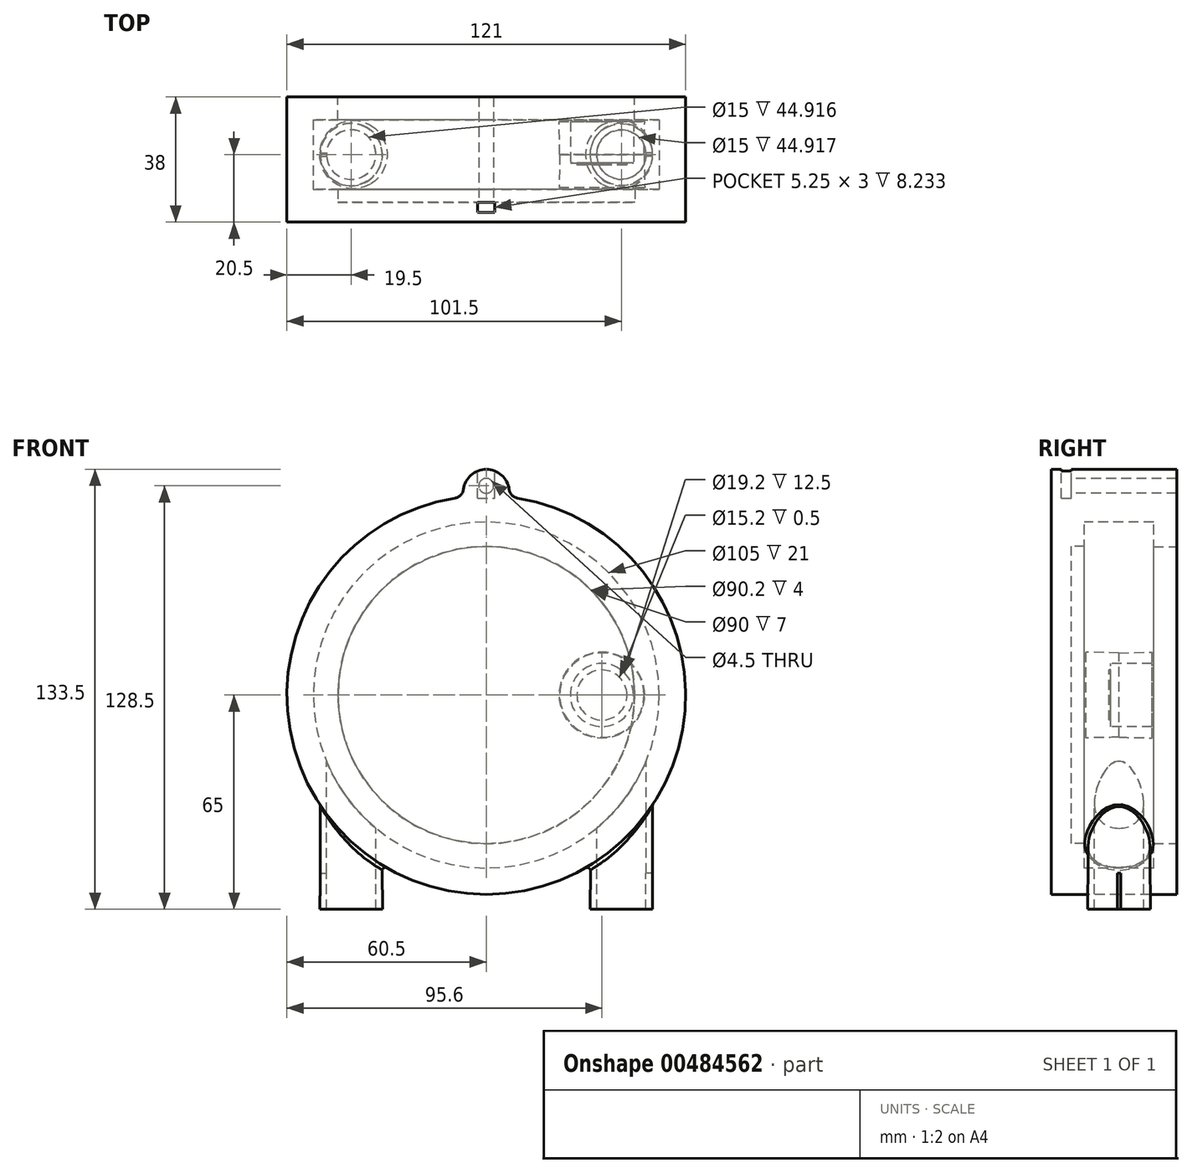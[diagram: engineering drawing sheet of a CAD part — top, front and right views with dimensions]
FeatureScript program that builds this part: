
annotation { "Feature Type Name" : "Feature", "Feature Type Description" : "" }
export const myFeature = defineFeature(function(context is Context, id is Id, definition is map)
    precondition{}
    {
        {
            var Q0;
            Q0=qCreatedBy(makeId("Top.planeOp"),FACE);
            var sketch = newSketch(context, id + "F0", { "sketchPlane" : qUnion([Q0])});
            skLineSegment(sketch, "E0", {"start": v(0, 0) * mm, "end": v(0, 21) * mm, "construction": true});
            skLineSegment(sketch, "E1", {"start": v(0, 28) * mm, "end": v(60.5, 28) * mm});
            skLineSegment(sketch, "E2", {"start": v(60.5, 28) * mm, "end": v(60.5, 21) * mm});
            skLineSegment(sketch, "E3", {"start": v(60.5, 21) * mm, "end": v(0, 21) * mm});
            skLineSegment(sketch, "E4", {"start": v(0, 28) * mm, "end": v(0, 21) * mm});
            skLineSegment(sketch, "E5", {"start": v(60.5, 21) * mm, "end": v(60.5, -10) * mm});
            skLineSegment(sketch, "E6", {"start": v(60.5, -10) * mm, "end": v(0, -10) * mm});
            skLineSegment(sketch, "E7", {"start": v(0, -10) * mm, "end": v(0, -4) * mm});
            skLineSegment(sketch, "E8", {"start": v(45.1, 0) * mm, "end": v(52.5, 0) * mm});
            skLineSegment(sketch, "E9", {"start": v(52.5, 0) * mm, "end": v(52.5, 21) * mm});
            skLineSegment(sketch, "E10", {"start": v(48.1, 0.5) * mm, "end": v(35.1, 0.5) * mm});
            skLineSegment(sketch, "E11", {"start": v(35.1, 0.5) * mm, "end": v(35.1, 7.5) * mm});
            skLineSegment(sketch, "E12", {"start": v(42.7, 8) * mm, "end": v(44.7, 8) * mm});
            skLineSegment(sketch, "E13", {"start": v(44.7, 8) * mm, "end": v(44.7, 20.5) * mm});
            skLineSegment(sketch, "E14", {"start": v(44.7, 20.5) * mm, "end": v(48.1, 20.5) * mm});
            skPoint(sketch, "E15", {"position": v(47.9, 10.5) * mm});
            skLineSegment(sketch, "E16", {"start": v(48.1, 20.5) * mm, "end": v(47.9, 10.5) * mm});
            skLineSegment(sketch, "E17", {"start": v(48.1, 0.5) * mm, "end": v(47.9, 10.5) * mm});
            skLineSegment(sketch, "E18", {"start": v(42.7, 8) * mm, "end": v(42.7, 7.5) * mm});
            skLineSegment(sketch, "E19", {"start": v(42.7, 7.5) * mm, "end": v(35.1, 7.5) * mm});
            skLineSegment(sketch, "E20", {"start": v(35.1, 7.5) * mm, "end": v(35.1, 11.5) * mm, "construction": true});
            skLineSegment(sketch, "E21", {"start": v(0, -4) * mm, "end": v(45.1, -4) * mm});
            skLineSegment(sketch, "E22", {"start": v(45.1, -4) * mm, "end": v(45.1, 0) * mm});
            skSolve(sketch);
        }
        {
            var Q0;
            {var subQ0=sQuery(id+"F0.wireOp",EDGE,"E5");Q0=makeQuery(id+"F0.imprint","IMPRINT",FACE,{"disambiguationData":[TD([[makeQuery(id+"F0.imprint","IMPRINT",EDGE,{"derivedFrom":subQ0}),-1.0]])]});}
            var Q1;
            Q1=sQuery(id+"F0.wireOp",EDGE,"E0");
            revolve(context, id + "F1", {"entities" : qUnion([Q0]), "axis" : qUnion([Q1]), "revolveType" : RevolveType.FULL});
        }
        {
            var Q0;
            Q0=makeQuery(id+"F0.imprint","IMPRINT",FACE,{"disambiguationData":[TD([[makeQuery(id+"F0.imprint","IMPRINT",EDGE,{"derivedFrom":sQuery(id+"F0.wireOp",EDGE,"E1")}),-1.0]])]});
            var Q1;
            Q1=sQuery(id+"F0.wireOp",EDGE,"E4");
            revolve(context, id + "F2", {"entities" : qUnion([Q0]), "axis" : qUnion([Q1]), "revolveType" : RevolveType.FULL});
        }
        {
            var Q0;
            {var subQ0=sQuery(id+"F0.wireOp",EDGE,"E3");Q0=makeQuery(id+"F1.opRevolve","SWEPT_FACE",FACE,{"disambiguationData":[OSD([subQ0]),TDD([makeQuery(id+"F0.imprint","IMPRINT",EDGE,{"disambiguationData":[TD([[makeQuery(id+"F0.imprint","INTERSECT",VERTEX,{"derivedFrom":[sQuery(id+"F0.wireOp",EDGE,"E2"),subQ0,sQuery(id+"F0.wireOp",EDGE,"E5")]}),-1.0]])],"derivedFrom":subQ0})])]});}
            var sketch = newSketch(context, id + "F3", { "sketchPlane" : qUnion([Q0])});
            skArc(sketch, "E23", {"start": v(6.95, 62.35) * mm, "mid": v(0, 68.5) * mm, "end": v(-6.95, 62.35) * mm});
            skArc(sketch, "E24", {"start": v(-9.46, 59.76) * mm, "mid": v(-7.77, 60.64) * mm, "end": v(-6.95, 62.35) * mm});
            skLineSegment(sketch, "E25", {"start": v(0, 0) * mm, "end": v(0, 56.73) * mm, "construction": true});
            skArc(sketch, "E26.MirrorCS", {"start": v(9.46, 59.76) * mm, "mid": v(7.77, 60.64) * mm, "end": v(6.95, 62.35) * mm});
            skArc(sketch, "E27", {"start": v(9.46, 59.76) * mm, "mid": v(0, 60.5) * mm, "end": v(-9.46, 59.76) * mm});
            skCircle(sketch, "E28", {"center": v(0, 63.5) * mm, "radius": 2.25 * mm});
            skSolve(sketch);
        }
        {
            var Q0;
            Q0=makeQuery(id+"F3.imprint","IMPRINT",FACE,{"disambiguationData":[TD([[makeQuery(id+"F3.imprint","IMPRINT",EDGE,{"derivedFrom":sQuery(id+"F3.wireOp",EDGE,"E23")}),1.0]])]});
            var Q1;
            Q1=makeQuery(id+"F2.opRevolve","SWEPT_FACE",FACE,{"disambiguationData":[OSD([sQuery(id+"F0.wireOp",EDGE,"E1")])]});
            extrude(context, id + "F4", {"entities" : qUnion([Q0]), "operationType" : NewBodyOperationType.ADD, "endBound" : BoundingType.UP_TO_SURFACE, "endBoundEntityFace" : qUnion([Q1]), "depth" : 25 * mm, "offsetDistance" : 25 * mm});
        }
        {
            var Q0;
            Q0=makeQuery(id+"F3.imprint","IMPRINT",FACE,{"disambiguationData":[TD([[makeQuery(id+"F3.imprint","IMPRINT",EDGE,{"derivedFrom":sQuery(id+"F3.wireOp",EDGE,"E23")}),1.0]])]});
            var Q1;
            Q1=makeQuery(id+"F3.imprint","IMPRINT",FACE,{"disambiguationData":[TD([[makeQuery(id+"F3.imprint","IMPRINT",EDGE,{"derivedFrom":sQuery(id+"F3.wireOp",EDGE,"E28")}),1.0]])]});
            var Q2;
            Q2=makeQuery(id+"F1.opRevolve","SWEPT_FACE",FACE,{"disambiguationData":[OSD([sQuery(id+"F0.wireOp",EDGE,"E6")])]});
            extrude(context, id + "F5", {"entities" : qUnion([Q0, Q1]), "operationType" : NewBodyOperationType.ADD, "endBound" : BoundingType.UP_TO_SURFACE, "oppositeDirection" : true, "endBoundEntityFace" : qUnion([Q2]), "depth" : 25 * mm, "offsetDistance" : 25 * mm});
        }
        {
            var Q0;
            Q0=sQuery(id+"F3.wireOp",EDGE,"E23");
            cPoint(context, id + "F6", {"entities" : qUnion([Q0]), "parameter" : 0.5});
        }
        {
            var Q0;
            Q0 = qCreatedBy(id + "F6" ,VERTEX);
            var Q1;
            Q1=sQuery(id+"F3.wireOp",EDGE,"E25");
            cPlane(context, id + "F7", {"entities" : qUnion([Q0, Q1]), "cplaneType" : CPlaneType.LINE_POINT, "offset" : 25 * mm, "width" : 150 * mm, "height" : 150 * mm});
        }
        {
            var Q0;
            Q0=qCreatedBy(id+"F7.planeOp",FACE);
            var sketch = newSketch(context, id + "F8", { "sketchPlane" : qUnion([Q0])});
            skLineSegment(sketch, "E29.bottom", {"start": v(-2.62, -7) * mm, "end": v(2.62, -7) * mm});
            skLineSegment(sketch, "E29.top", {"start": v(-2.62, -4) * mm, "end": v(2.62, -4) * mm});
            skLineSegment(sketch, "E29.left", {"start": v(-2.62, -7) * mm, "end": v(-2.62, -4) * mm});
            skLineSegment(sketch, "E29.right", {"start": v(2.63, -7) * mm, "end": v(2.63, -4) * mm});
            skLineSegment(sketch, "E30", {"start": v(0, -4) * mm, "end": v(0, 0) * mm, "construction": true});
            skSolve(sketch);
        }
        {
            var Q0;
            Q0 = qSketchRegion(id + "F8", true);
            var Q1;
            Q1=makeQuery(id+"F5.opExtrude","CAP_VERTEX",VERTEX,{"disambiguationData":[OSD([sQuery(id+"F0.wireOp",EDGE,"E2"),sQuery(id+"F0.wireOp",EDGE,"E3"),sQuery(id+"F0.wireOp",EDGE,"E5"),sQuery(id+"F0.wireOp",EDGE,"E6"),sQuery(id+"F3.wireOp",EDGE,"E24"),sQuery(id+"F3.wireOp",EDGE,"E27")])],"isStart":false});
            extrude(context, id + "F9", {"entities" : qUnion([Q0]), "operationType" : NewBodyOperationType.REMOVE, "endBound" : BoundingType.UP_TO_VERTEX, "oppositeDirection" : true, "endBoundEntityVertex" : qUnion([Q1]), "depth" : 8 * mm});
        }
        {
            var Q0;
            Q0=makeQuery(id+"F3.imprint","IMPRINT",FACE,{"disambiguationData":[TD([[makeQuery(id+"F3.imprint","IMPRINT",EDGE,{"derivedFrom":sQuery(id+"F3.wireOp",EDGE,"E28")}),1.0]])]});
            var Q1;
            Q1=makeQuery(id+"F9.boolean.opBoolean","COPY",FACE,{"derivedFrom":makeQuery(id+"F9.opExtrude","SWEPT_FACE",FACE,{"disambiguationData":[OSD([sQuery(id+"F8.wireOp",EDGE,"E29.top")])]})});
            extrude(context, id + "F10", {"entities" : qUnion([Q0]), "operationType" : NewBodyOperationType.REMOVE, "endBound" : BoundingType.UP_TO_SURFACE, "oppositeDirection" : true, "depth" : 25 * mm, "endBoundEntityFace" : qUnion([Q1]), "offsetDistance" : 25 * mm});
        }
        {
            var Q0;
            Q0=sQuery(id+"F0.wireOp",EDGE,"E0");
            cPoint(context, id + "F11", {"entities" : qUnion([Q0]), "parameter" : 0.5});
        }
        {
            var Q0;
            Q0 = qCreatedBy(id + "F11" ,VERTEX);
            var Q1;
            Q1=sQuery(id+"F0.wireOp",EDGE,"E0");
            cPlane(context, id + "F12", {"entities" : qUnion([Q0, Q1]), "cplaneType" : CPlaneType.LINE_POINT, "offset" : 25 * mm, "width" : 150 * mm, "height" : 150 * mm});
        }
        {
            var Q0;
            {var subQ0=sQuery(id+"F0.wireOp",EDGE,"E1");Q0=makeQuery(id+"F8Ouq5LeF6Cl571_2.3.F4.boolean.opBoolean","MERGE",FACE,{"derivedFrom":[makeQuery(id+"F8Ouq5LeF6Cl571_2.2.F4.boolean.opBoolean","MERGE",FACE,{"derivedFrom":[makeQuery(id+"F8Ouq5LeF6Cl571_2.1.F4.boolean.opBoolean","MERGE",FACE,{"derivedFrom":[makeQuery(id+"F4.boolean.opBoolean","MERGE",FACE,{"derivedFrom":[makeQuery(id+"F2.opRevolve","SWEPT_FACE",FACE,{"disambiguationData":[OSD([subQ0])]}),makeQuery(id+"F4.opExtrude","CAP_FACE",FACE,{"disambiguationData":[OSD([subQ0])],"isStart":false})]}),makeQuery(id+"F8Ouq5LeF6Cl571_2.1.F4.opExtrude","CAP_FACE",FACE,{"disambiguationData":[OSD([subQ0])],"isStart":false})]}),makeQuery(id+"F8Ouq5LeF6Cl571_2.2.F4.opExtrude","CAP_FACE",FACE,{"disambiguationData":[OSD([subQ0])],"isStart":false})]}),makeQuery(id+"F8Ouq5LeF6Cl571_2.3.F4.opExtrude","CAP_FACE",FACE,{"disambiguationData":[OSD([subQ0])],"isStart":false})]});}
            var sketch = newSketch(context, id + "F13", { "sketchPlane" : qUnion([Q0])});
            skCircle(sketch, "E31", {"center": v(0, 0) * mm, "radius": 45 * mm});
            skSolve(sketch);
        }
        {
            var Q0;
            Q0=makeQuery(id+"F13.imprint","IMPRINT",FACE,{"disambiguationData":[TD([[makeQuery(id+"F13.imprint","IMPRINT",EDGE,{"derivedFrom":sQuery(id+"F13.wireOp",EDGE,"E31")}),1.0]])]});
            extrude(context, id + "F14", {"entities" : qUnion([Q0]), "operationType" : NewBodyOperationType.REMOVE, "endBound" : BoundingType.UP_TO_NEXT, "oppositeDirection" : true, "depth" : 25 * mm, "offsetDistance" : 25 * mm});
        }
        {
            var Q0;
            Q0=qCreatedBy(id+"F12.planeOp",FACE);
            var sketch = newSketch(context, id + "F15", { "sketchPlane" : qUnion([Q0])});
            skLineSegment(sketch, "E32", {"start": v(-50.39, -50) * mm, "end": v(-41, -50) * mm});
            skLineSegment(sketch, "E33", {"start": v(-41, -50) * mm, "end": v(-41, -65) * mm, "construction": true});
            skLineSegment(sketch, "E34", {"start": v(-41, -65) * mm, "end": v(-50.5, -65) * mm});
            skLineSegment(sketch, "E35", {"start": v(-50.5, -65) * mm, "end": v(-50.39, -50) * mm});
            skLineSegment(sketch, "E36", {"start": v(-41, -65) * mm, "end": v(-41, -50) * mm});
            skLineSegment(sketch, "E37", {"start": v(-48.5, -50) * mm, "end": v(-48.5, -65) * mm});
            skSolve(sketch);
        }
        {
            var Q0;
            Q0=makeQuery(id+"F15.imprint","IMPRINT",FACE,{"disambiguationData":[TD([[makeQuery(id+"F15.imprint","IMPRINT",EDGE,{"derivedFrom":sQuery(id+"F15.wireOp",EDGE,"E32")}),-1.0]])]});
            var Q1;
            Q1=sQuery(id+"F15.wireOp",EDGE,"E35");
            var Q2;
            Q2=sQuery(id+"F15.wireOp",EDGE,"E32");
            var Q3;
            Q3=sQuery(id+"F15.wireOp",EDGE,"E34");
            var Q4;
            Q4=sQuery(id+"F15.wireOp",EDGE,"E33");
            revolve(context, id + "F16", {"operationType" : NewBodyOperationType.ADD, "entities" : qUnion([Q0]), "surfaceEntities" : qUnion([Q1, Q2, Q3]), "axis" : qUnion([Q4]), "revolveType" : RevolveType.FULL});
        }
        {
            var Q0;
            Q0=makeQuery(id+"F16.opRevolve","SWEPT_FACE",FACE,{"disambiguationData":[OSD([sQuery(id+"F15.wireOp",EDGE,"E32")])]});
            var Q1;
            Q1=makeQuery(id+"F1.opRevolve","SWEPT_FACE",FACE,{"disambiguationData":[OSD([sQuery(id+"F0.wireOp",EDGE,"E9")])]});
            extrude(context, id + "F17", {"entities" : qUnion([Q0]), "operationType" : NewBodyOperationType.ADD, "endBound" : BoundingType.UP_TO_SURFACE, "depth" : 25 * mm, "endBoundEntityFace" : qUnion([Q1]), "offsetDistance" : 25 * mm});
        }
        {
            var Q0;
            Q0=makeQuery(id+"F16.opRevolve","SWEPT_FACE",FACE,{"disambiguationData":[OSD([sQuery(id+"F15.wireOp",EDGE,"E34")])]});
            var sketch = newSketch(context, id + "F18", { "sketchPlane" : qUnion([Q0])});
            skLineSegment(sketch, "E38.bottom", {"start": v(50.5, -10) * mm, "end": v(41, -10) * mm});
            skLineSegment(sketch, "E38.top", {"start": v(50.5, -11) * mm, "end": v(41, -11) * mm});
            skLineSegment(sketch, "E38.left", {"start": v(50.5, -10) * mm, "end": v(50.5, -11) * mm});
            skLineSegment(sketch, "E38.right", {"start": v(41, -10) * mm, "end": v(41, -11) * mm});
            skSolve(sketch);
        }
        {
            var Q0;
            {var subQ0=sQuery(id+"F15.wireOp",EDGE,"E36");Q0=makeQuery(id+"F15.imprint","IMPRINT",FACE,{"disambiguationData":[TD([[makeQuery(id+"F15.imprint","IMPRINT",EDGE,{"derivedFrom":subQ0}),1.0]])]});}
            var Q1;
            Q1=sQuery(id+"F15.wireOp",EDGE,"E36");
            revolve(context, id + "F19", {"operationType" : NewBodyOperationType.REMOVE, "entities" : qUnion([Q0]), "axis" : qUnion([Q1]), "revolveType" : RevolveType.FULL, "oppositeDirection" : true});
        }
        {
            var Q0;
            Q0=makeQuery(id+"F19.boolean.opBoolean","COPY",FACE,{"derivedFrom":makeQuery(id+"F19.opRevolve","SWEPT_FACE",FACE,{"disambiguationData":[OSD([sQuery(id+"F15.wireOp",EDGE,"E32")])]})});
            extrude(context, id + "F20", {"entities" : qUnion([Q0]), "operationType" : NewBodyOperationType.REMOVE, "endBound" : BoundingType.UP_TO_NEXT, "oppositeDirection" : true, "depth" : 25 * mm, "offsetDistance" : 25 * mm});
        }
        {
            var Q0;
            {var subQ4=sQuery(id+"F18.wireOp",EDGE,"E38.right");Q0=makeQuery(id+"F18.imprint","IMPRINT",FACE,{"disambiguationData":[TD([[makeQuery(id+"F18.imprint","IMPRINT",EDGE,{"derivedFrom":subQ4}),1.0]])]});}
            extrude(context, id + "F21", {"entities" : qUnion([Q0]), "operationType" : NewBodyOperationType.REMOVE, "oppositeDirection" : true, "depth" : 11 * mm, "offsetDistance" : 25 * mm});
        }
        {
            var Q0;
            {var subQ1=sQuery(id+"F3.wireOp",EDGE,"E26.MirrorCS");var subQ2=sQuery(id+"F3.wireOp",EDGE,"E24");var subQ10=makeQuery(id+"F8Ouq5LeF6Cl571_2.1.F5.opExtrude","SWEPT_FACE",FACE,{"disambiguationData":[OSD([subQ2])]});Q0=makeQuery(id+"F17.boolean.opBoolean","INTERSECT",EDGE,{"derivedFrom":[makeQuery(id+"F8Ouq5LeF6Cl571_2.2.F5.boolean.opBoolean","SPLIT",FACE,{"disambiguationData":[TD([subQ10])],"derivedFrom":makeQuery(id+"F8Ouq5LeF6Cl571_2.1.F5.boolean.opBoolean","SPLIT",FACE,{"disambiguationData":[TD([makeQuery(id+"F5.opExtrude","SWEPT_FACE",FACE,{"disambiguationData":[OSD([subQ1])]})])],"derivedFrom":makeQuery(id+"F1.opRevolve","SWEPT_FACE",FACE,{"disambiguationData":[OSD([sQuery(id+"F0.wireOp",EDGE,"E5")])]})})}),makeQuery(id+"F17.opExtrude","SWEPT_FACE",FACE,{"disambiguationData":[OSD([sQuery(id+"F15.wireOp",EDGE,"E32"),sQuery(id+"F15.wireOp",EDGE,"E35")])]})]});}
            fillet(context, id + "F22", {"entities" : qUnion([Q0]), "radius" : 1 * mm, "tangentPropagation" : true, "allowEdgeOverflow" : false});
        }
        {
            var Q0;
            Q0=makeQuery(id+"F16.opRevolve","SWEPT_FACE",FACE,{"disambiguationData":[OSD([sQuery(id+"F15.wireOp",EDGE,"E35")])]});
            var Q1;
            Q1=makeQuery(id+"FTRnezzPuA4SQwe_3.1.F21.boolean.opBoolean","COPY",FACE,{"derivedFrom":makeQuery(id+"FTRnezzPuA4SQwe_3.1.F21.opExtrude","SWEPT_FACE",FACE,{"disambiguationData":[OSD([sQuery(id+"F18.wireOp",EDGE,"E38.bottom")])]})});
            var Q2;
            Q2=makeQuery(id+"F17.opExtrude","SWEPT_FACE",FACE,{"disambiguationData":[OSD([sQuery(id+"F15.wireOp",EDGE,"E32"),sQuery(id+"F15.wireOp",EDGE,"E35")])]});
            var Q3;
            Q3=makeQuery(id+"F22.opFillet","BLEND_FACE",FACE,{"disambiguationData":[OSD([sQuery(id+"F0.wireOp",EDGE,"E5"),sQuery(id+"F15.wireOp",EDGE,"E32"),sQuery(id+"F15.wireOp",EDGE,"E35")])]});
            var Q4;
            Q4=makeQuery(id+"FTRnezzPuA4SQwe_3.3.F21.boolean.opBoolean","COPY",FACE,{"derivedFrom":makeQuery(id+"FTRnezzPuA4SQwe_3.3.F21.opExtrude","SWEPT_FACE",FACE,{"disambiguationData":[OSD([sQuery(id+"F18.wireOp",EDGE,"E38.top")])]})});
            var Q5;
            Q5=makeQuery(id+"FTRnezzPuA4SQwe_3.1.F21.boolean.opBoolean","COPY",FACE,{"derivedFrom":makeQuery(id+"FTRnezzPuA4SQwe_3.1.F21.opExtrude","SWEPT_FACE",FACE,{"disambiguationData":[OSD([sQuery(id+"F18.wireOp",EDGE,"E38.top")])]})});
            var Q6;
            {var subQ0=makeQuery(id+"FTRnezzPuA4SQwe_3.1.F21.opExtrude","SWEPT_FACE",FACE,{"disambiguationData":[OSD([sQuery(id+"F18.wireOp",EDGE,"E38.top")])]});var subQ5=sQuery(id+"F18.wireOp",EDGE,"E38.bottom");Q6=makeQuery(id+"FTRnezzPuA4SQwe_3.2.F21.boolean.opBoolean","SPLIT",FACE,{"disambiguationData":[TD([makeQuery(id+"FTRnezzPuA4SQwe_3.1.F21.boolean.opBoolean","COPY",FACE,{"derivedFrom":subQ0})])],"derivedFrom":makeQuery(id+"FTRnezzPuA4SQwe_3.1.F21.boolean.opBoolean","SPLIT",FACE,{"disambiguationData":[TD([makeQuery(id+"F21.boolean.opBoolean","COPY",FACE,{"derivedFrom":makeQuery(id+"F21.opExtrude","SWEPT_FACE",FACE,{"disambiguationData":[OSD([subQ5])]})})])],"derivedFrom":makeQuery(id+"F16.opRevolve","SWEPT_FACE",FACE,{"disambiguationData":[OSD([sQuery(id+"F15.wireOp",EDGE,"E34")])]})})});}
            var Q7;
            Q7=makeQuery(id+"F21.boolean.opBoolean","COPY",FACE,{"derivedFrom":makeQuery(id+"F21.opExtrude","SWEPT_FACE",FACE,{"disambiguationData":[OSD([sQuery(id+"F18.wireOp",EDGE,"E38.top")])]})});
            var Q8;
            Q8=makeQuery(id+"FTRnezzPuA4SQwe_3.1.F21.boolean.opBoolean","SPLIT",FACE,{"disambiguationData":[TD([makeQuery(id+"F21.boolean.opBoolean","COPY",FACE,{"derivedFrom":makeQuery(id+"F21.opExtrude","SWEPT_FACE",FACE,{"disambiguationData":[OSD([sQuery(id+"F18.wireOp",EDGE,"E38.top")])]})})])],"derivedFrom":makeQuery(id+"F16.opRevolve","SWEPT_FACE",FACE,{"disambiguationData":[OSD([sQuery(id+"F15.wireOp",EDGE,"E34")])]})});
            var Q9;
            Q9=makeQuery(id+"FTRnezzPuA4SQwe_3.3.F21.boolean.opBoolean","COPY",FACE,{"derivedFrom":makeQuery(id+"FTRnezzPuA4SQwe_3.3.F21.opExtrude","SWEPT_FACE",FACE,{"disambiguationData":[OSD([sQuery(id+"F18.wireOp",EDGE,"E38.bottom")])]})});
            var Q10;
            Q10=makeQuery(id+"FTRnezzPuA4SQwe_3.2.F21.boolean.opBoolean","COPY",FACE,{"derivedFrom":makeQuery(id+"FTRnezzPuA4SQwe_3.2.F21.opExtrude","SWEPT_FACE",FACE,{"disambiguationData":[OSD([sQuery(id+"F18.wireOp",EDGE,"E38.top")])]})});
            var Q11;
            {var subQ0=makeQuery(id+"F21.boolean.opBoolean","COPY",FACE,{"derivedFrom":makeQuery(id+"F21.opExtrude","SWEPT_FACE",FACE,{"disambiguationData":[OSD([sQuery(id+"F18.wireOp",EDGE,"E38.bottom")])]})});Q11=makeQuery(id+"FTRnezzPuA4SQwe_3.3.F21.boolean.opBoolean","SPLIT",FACE,{"disambiguationData":[TD([subQ0])],"derivedFrom":makeQuery(id+"FTRnezzPuA4SQwe_3.2.F21.boolean.opBoolean","SPLIT",FACE,{"disambiguationData":[TD([subQ0])],"derivedFrom":makeQuery(id+"FTRnezzPuA4SQwe_3.1.F21.boolean.opBoolean","SPLIT",FACE,{"disambiguationData":[TD([subQ0])],"derivedFrom":makeQuery(id+"F16.opRevolve","SWEPT_FACE",FACE,{"disambiguationData":[OSD([sQuery(id+"F15.wireOp",EDGE,"E34")])]})})})});}
            var Q12;
            {var subQ3=sQuery(id+"F18.wireOp",EDGE,"E38.top");var subQ4=makeQuery(id+"FTRnezzPuA4SQwe_3.2.F21.opExtrude","SWEPT_FACE",FACE,{"disambiguationData":[OSD([subQ3])]});var subQ6=sQuery(id+"F18.wireOp",EDGE,"E38.bottom");var subQ7=makeQuery(id+"F21.boolean.opBoolean","COPY",FACE,{"derivedFrom":makeQuery(id+"F21.opExtrude","SWEPT_FACE",FACE,{"disambiguationData":[OSD([subQ6])]})});Q12=makeQuery(id+"FTRnezzPuA4SQwe_3.3.F21.boolean.opBoolean","SPLIT",FACE,{"disambiguationData":[TD([makeQuery(id+"FTRnezzPuA4SQwe_3.2.F21.boolean.opBoolean","COPY",FACE,{"derivedFrom":subQ4})])],"derivedFrom":makeQuery(id+"FTRnezzPuA4SQwe_3.2.F21.boolean.opBoolean","SPLIT",FACE,{"disambiguationData":[TD([subQ7])],"derivedFrom":makeQuery(id+"FTRnezzPuA4SQwe_3.1.F21.boolean.opBoolean","SPLIT",FACE,{"disambiguationData":[TD([subQ7])],"derivedFrom":makeQuery(id+"F16.opRevolve","SWEPT_FACE",FACE,{"disambiguationData":[OSD([sQuery(id+"F15.wireOp",EDGE,"E34")])]})})})});}
            var Q13;
            Q13=makeQuery(id+"F21.boolean.opBoolean","COPY",FACE,{"derivedFrom":makeQuery(id+"F21.opExtrude","SWEPT_FACE",FACE,{"disambiguationData":[OSD([sQuery(id+"F18.wireOp",EDGE,"E38.bottom")])]})});
            var Q14;
            Q14=makeQuery(id+"F21.boolean.opBoolean","COPY",FACE,{"derivedFrom":makeQuery(id+"F21.opExtrude","CAP_FACE",FACE,{"disambiguationData":[OSD([sQuery(id+"F15.wireOp",EDGE,"E34"),sQuery(id+"F15.wireOp",EDGE,"E35"),sQuery(id+"F18.wireOp",EDGE,"E38.bottom"),sQuery(id+"F18.wireOp",EDGE,"E38.top"),sQuery(id+"F18.wireOp",EDGE,"E38.right")])],"isStart":false})});
            var Q15;
            Q15=makeQuery(id+"FTRnezzPuA4SQwe_3.2.F21.boolean.opBoolean","COPY",FACE,{"derivedFrom":makeQuery(id+"FTRnezzPuA4SQwe_3.2.F21.opExtrude","SWEPT_FACE",FACE,{"disambiguationData":[OSD([sQuery(id+"F18.wireOp",EDGE,"E38.bottom")])]})});
            var Q16;
            Q16=makeQuery(id+"FTRnezzPuA4SQwe_3.2.F21.boolean.opBoolean","COPY",FACE,{"derivedFrom":makeQuery(id+"FTRnezzPuA4SQwe_3.2.F21.opExtrude","CAP_FACE",FACE,{"disambiguationData":[OSD([sQuery(id+"F15.wireOp",EDGE,"E34"),sQuery(id+"F15.wireOp",EDGE,"E35"),sQuery(id+"F18.wireOp",EDGE,"E38.bottom"),sQuery(id+"F18.wireOp",EDGE,"E38.top"),sQuery(id+"F18.wireOp",EDGE,"E38.right")])],"isStart":false})});
            var Q17;
            Q17=makeQuery(id+"FTRnezzPuA4SQwe_3.1.F21.boolean.opBoolean","COPY",FACE,{"derivedFrom":makeQuery(id+"FTRnezzPuA4SQwe_3.1.F21.opExtrude","CAP_FACE",FACE,{"disambiguationData":[OSD([sQuery(id+"F15.wireOp",EDGE,"E34"),sQuery(id+"F15.wireOp",EDGE,"E35"),sQuery(id+"F18.wireOp",EDGE,"E38.bottom"),sQuery(id+"F18.wireOp",EDGE,"E38.top"),sQuery(id+"F18.wireOp",EDGE,"E38.right")])],"isStart":false})});
            var Q18;
            Q18=makeQuery(id+"FTRnezzPuA4SQwe_3.3.F21.boolean.opBoolean","COPY",FACE,{"derivedFrom":makeQuery(id+"FTRnezzPuA4SQwe_3.3.F21.opExtrude","CAP_FACE",FACE,{"disambiguationData":[OSD([sQuery(id+"F15.wireOp",EDGE,"E34"),sQuery(id+"F15.wireOp",EDGE,"E35"),sQuery(id+"F18.wireOp",EDGE,"E38.bottom"),sQuery(id+"F18.wireOp",EDGE,"E38.top"),sQuery(id+"F18.wireOp",EDGE,"E38.right")])],"isStart":false})});
            var Q19;
            {var subQ0=sQuery(id+"F15.wireOp",EDGE,"E37");Q19=makeQuery(id+"F20.boolean.opBoolean","MERGE",FACE,{"derivedFrom":[makeQuery(id+"F19.boolean.opBoolean","COPY",FACE,{"derivedFrom":makeQuery(id+"F19.opRevolve","SWEPT_FACE",FACE,{"disambiguationData":[OSD([subQ0])]})}),makeQuery(id+"F20.opExtrude","SWEPT_FACE",FACE,{"disambiguationData":[OSD([sQuery(id+"F15.wireOp",EDGE,"E32"),subQ0])]})]});}
            var Q20;
            Q20=qCreatedBy(makeId("Right.planeOp"),FACE);
            mirror(context, id + "F23", {"patternType" : MirrorType.FACE, "faces" : qUnion([Q0, Q1, Q2, Q3, Q4, Q5, Q6, Q7, Q8, Q9, Q10, Q11, Q12, Q13, Q14, Q15, Q16, Q17, Q18, Q19]), "mirrorPlane" : qUnion([Q20])});
        }
        {
            var Q0;
            Q0=makeQuery(id+"F0.imprint","IMPRINT",FACE,{"disambiguationData":[TD([[makeQuery(id+"F0.imprint","IMPRINT",EDGE,{"derivedFrom":sQuery(id+"F0.wireOp",EDGE,"E10")}),-1.0]])]});
            var Q1;
            Q1=sQuery(id+"F0.wireOp",EDGE,"E20");
            revolve(context, id + "F24", {"entities" : qUnion([Q0]), "axis" : qUnion([Q1]), "revolveType" : RevolveType.FULL});
        }
    });
